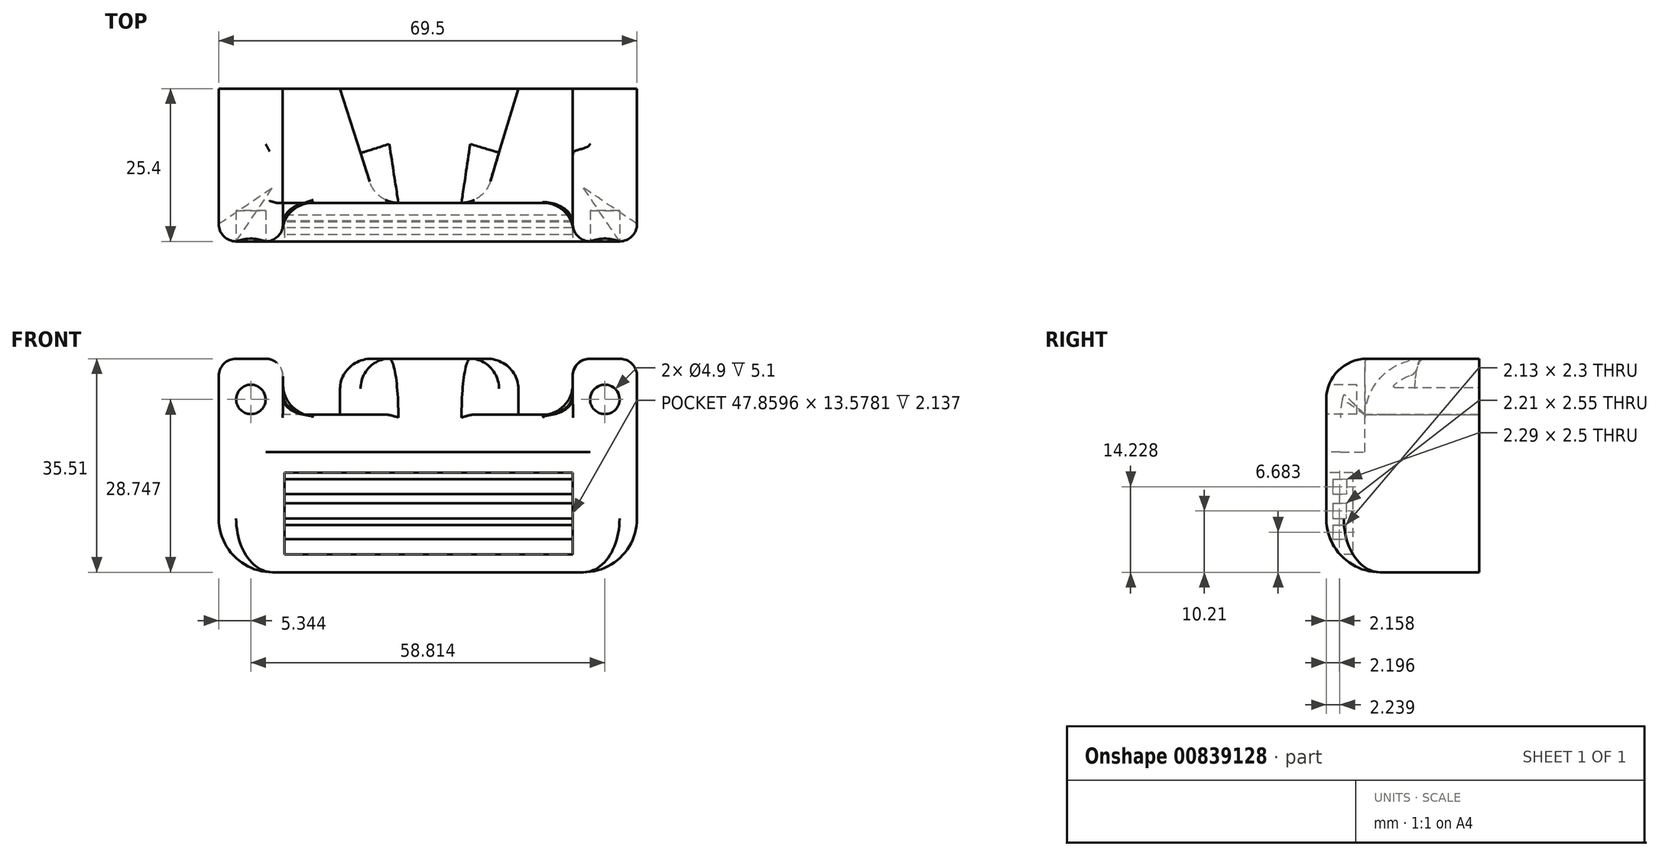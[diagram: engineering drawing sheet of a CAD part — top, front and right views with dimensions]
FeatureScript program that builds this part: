
annotation { "Feature Type Name" : "Feature", "Feature Type Description" : "" }
export const myFeature = defineFeature(function(context is Context, id is Id, definition is map)
    precondition{}
    {
        {
            var Q0;
            Q0=qCreatedBy(makeId("Front.planeOp"),FACE);
            var sketch = newSketch(context, id + "F0", { "sketchPlane" : qUnion([Q0])});
            skLineSegment(sketch, "E0.bottom", {"start": v(-27.6, 7.03) * mm, "end": v(41.91, 7.03) * mm});
            skLineSegment(sketch, "E0.top", {"start": v(-27.6, -12.98) * mm, "end": v(41.91, -12.98) * mm});
            skLineSegment(sketch, "E0.left", {"start": v(-27.6, 7.03) * mm, "end": v(-27.6, -12.98) * mm});
            skLineSegment(sketch, "E0.right", {"start": v(41.91, 7.03) * mm, "end": v(41.91, -12.98) * mm});
            skSolve(sketch);
        }
        {
            var Q0;
            Q0=makeQuery(id+"F0.imprint","IMPRINT",FACE,{"disambiguationData":[TD([[makeQuery(id+"F0.imprint","IMPRINT",EDGE,{"derivedFrom":sQuery(id+"F0.wireOp",EDGE,"E0.bottom")}),-1.0]])]});
            extrude(context, id + "F1", {"entities" : qUnion([Q0]), "depth" : 25.4 * mm, "offsetDistance" : 25.4 * mm});
        }
        {
            var Q0;
            Q0=makeQuery(id+"F1.opExtrude","SWEPT_FACE",FACE,{"disambiguationData":[OSD([sQuery(id+"F0.wireOp",EDGE,"E0.bottom")])]});
            var sketch = newSketch(context, id + "F2", { "sketchPlane" : qUnion([Q0])});
            skLineSegment(sketch, "E1.bottom", {"start": v(-16.9, 0) * mm, "end": v(31.22, 0) * mm});
            skLineSegment(sketch, "E1.top", {"start": v(-16.9, -19) * mm, "end": v(31.22, -19) * mm});
            skLineSegment(sketch, "E1.left", {"start": v(-16.9, 0) * mm, "end": v(-16.9, -19) * mm});
            skLineSegment(sketch, "E1.right", {"start": v(31.22, 0) * mm, "end": v(31.22, -19) * mm});
            skLineSegment(sketch, "E2.bottom", {"start": v(-27.6, 0) * mm, "end": v(-16.9, 0) * mm});
            skLineSegment(sketch, "E2.top", {"start": v(-27.6, -25.4) * mm, "end": v(-16.9, -25.4) * mm});
            skLineSegment(sketch, "E2.left", {"start": v(-27.6, 0) * mm, "end": v(-27.6, -25.4) * mm});
            skLineSegment(sketch, "E2.right", {"start": v(-16.9, 0) * mm, "end": v(-16.9, -25.4) * mm});
            skLineSegment(sketch, "E3.bottom", {"start": v(31.22, 0) * mm, "end": v(41.91, 0) * mm});
            skLineSegment(sketch, "E3.top", {"start": v(31.22, -25.4) * mm, "end": v(41.91, -25.4) * mm});
            skLineSegment(sketch, "E3.left", {"start": v(31.22, 0) * mm, "end": v(31.22, -25.4) * mm});
            skLineSegment(sketch, "E3.right", {"start": v(41.91, 0) * mm, "end": v(41.91, -25.4) * mm});
            skSolve(sketch);
        }
        {
            var Q0;
            {var subQ1=sQuery(id+"F2.wireOp",EDGE,"E2.bottom");Q0=makeQuery(id+"F2.imprint","IMPRINT",FACE,{"disambiguationData":[TD([[makeQuery(id+"F2.imprint","IMPRINT",EDGE,{"derivedFrom":subQ1}),-1.0]])]});}
            var Q1;
            {var subQ0=sQuery(id+"F2.wireOp",EDGE,"E1.bottom");Q1=makeQuery(id+"F2.imprint","IMPRINT",FACE,{"disambiguationData":[TD([[makeQuery(id+"F2.imprint","IMPRINT",EDGE,{"derivedFrom":subQ0}),-1.0]])]});}
            var Q2;
            {var subQ3=sQuery(id+"F2.wireOp",EDGE,"E3.bottom");Q2=makeQuery(id+"F2.imprint","IMPRINT",FACE,{"disambiguationData":[TD([[makeQuery(id+"F2.imprint","IMPRINT",EDGE,{"derivedFrom":subQ3}),-1.0]])]});}
            extrude(context, id + "F3", {"entities" : qUnion([Q0, Q1, Q2]), "operationType" : NewBodyOperationType.ADD, "depth" : 15.5 * mm, "offsetDistance" : 25.4 * mm});
        }
        {
            var Q0;
            Q0=makeQuery(id+"F3.opExtrude","CAP_EDGE",EDGE,{"disambiguationData":[OSD([sQuery(id+"F2.wireOp",EDGE,"E2.top")])],"isStart":false});
            var Q1;
            Q1=makeQuery(id+"F3.opExtrude","CAP_EDGE",EDGE,{"disambiguationData":[OSD([sQuery(id+"F2.wireOp",EDGE,"E3.top")])],"isStart":false});
            fillet(context, id + "F4", {"entities" : qUnion([Q0, Q1]), "radius" : 6.76 * mm, "tangentPropagation" : true, "allowEdgeOverflow" : false});
        }
        {
            var Q0;
            Q0=makeQuery(id+"F4.opFillet","BLEND_EDGE",EDGE,{"blendedFrom":[makeQuery(id+"F3.opExtrude","CAP_EDGE",EDGE,{"disambiguationData":[OSD([sQuery(id+"F2.wireOp",EDGE,"E2.top")])],"isStart":false}),makeQuery(id+"F3.boolean.opBoolean","MERGE",FACE,{"derivedFrom":[makeQuery(id+"F1.opExtrude","SWEPT_FACE",FACE,{"disambiguationData":[OSD([sQuery(id+"F0.wireOp",EDGE,"E0.left")])]}),makeQuery(id+"F3.opExtrude","SWEPT_FACE",FACE,{"disambiguationData":[OSD([sQuery(id+"F2.wireOp",EDGE,"E2.left")])]})]})],"blendedInto":[makeQuery(id+"F3.boolean.opBoolean","MERGE",FACE,{"derivedFrom":[makeQuery(id+"F1.opExtrude","SWEPT_FACE",FACE,{"disambiguationData":[OSD([sQuery(id+"F0.wireOp",EDGE,"E0.left")])]}),makeQuery(id+"F3.opExtrude","SWEPT_FACE",FACE,{"disambiguationData":[OSD([sQuery(id+"F2.wireOp",EDGE,"E2.left")])]})]})]});
            var Q1;
            Q1=makeQuery(id+"F3.boolean.opBoolean","MERGE",EDGE,{"derivedFrom":[makeQuery(id+"F1.opExtrude","CAP_EDGE",EDGE,{"disambiguationData":[OSD([sQuery(id+"F0.wireOp",EDGE,"E0.right")])],"isStart":false}),makeQuery(id+"F3.opExtrude","SWEPT_EDGE",EDGE,{"disambiguationData":[OSD([sQuery(id+"F2.wireOp",EDGE,"E3.top"),sQuery(id+"F2.wireOp",EDGE,"E3.right")])]})]});
            fillet(context, id + "F5", {"entities" : qUnion([Q0, Q1]), "radius" : 2.9 * mm, "tangentPropagation" : true, "allowEdgeOverflow" : false});
        }
        {
            var Q0;
            Q0=makeQuery(id+"F4.opFillet","BLEND_EDGE",EDGE,{"blendedFrom":[makeQuery(id+"F3.opExtrude","CAP_EDGE",EDGE,{"disambiguationData":[OSD([sQuery(id+"F2.wireOp",EDGE,"E2.top")])],"isStart":false}),makeQuery(id+"F3.opExtrude","SWEPT_FACE",FACE,{"disambiguationData":[OSD([sQuery(id+"F2.wireOp",EDGE,"E1.top")])]})],"blendedInto":[makeQuery(id+"F3.opExtrude","SWEPT_FACE",FACE,{"disambiguationData":[OSD([sQuery(id+"F2.wireOp",EDGE,"E1.top")])]})]});
            fillet(context, id + "F6", {"entities" : qUnion([Q0]), "radius" : 9.79 * mm, "tangentPropagation" : true, "allowEdgeOverflow" : false});
        }
        {
            var Q0;
            Q0=makeQuery(id+"F4.opFillet","BLEND_EDGE",EDGE,{"blendedFrom":[makeQuery(id+"F3.opExtrude","CAP_EDGE",EDGE,{"disambiguationData":[OSD([sQuery(id+"F2.wireOp",EDGE,"E2.top")])],"isStart":false}),makeQuery(id+"F3.opExtrude","SWEPT_FACE",FACE,{"disambiguationData":[OSD([sQuery(id+"F2.wireOp",EDGE,"E2.right")])]})],"blendedInto":[makeQuery(id+"F3.opExtrude","SWEPT_FACE",FACE,{"disambiguationData":[OSD([sQuery(id+"F2.wireOp",EDGE,"E2.right")])]})]});
            var Q1;
            Q1=makeQuery(id+"F4.opFillet","BLEND_EDGE",EDGE,{"blendedFrom":[makeQuery(id+"F3.opExtrude","CAP_EDGE",EDGE,{"disambiguationData":[OSD([sQuery(id+"F2.wireOp",EDGE,"E2.top")])],"isStart":false}),makeQuery(id+"F3.opExtrude","SWEPT_FACE",FACE,{"disambiguationData":[OSD([sQuery(id+"F2.wireOp",EDGE,"E3.left")])]})],"blendedInto":[makeQuery(id+"F3.opExtrude","SWEPT_FACE",FACE,{"disambiguationData":[OSD([sQuery(id+"F2.wireOp",EDGE,"E3.left")])]})]});
            fillet(context, id + "F7", {"entities" : qUnion([Q0, Q1]), "radius" : 2.9 * mm, "tangentPropagation" : true, "allowEdgeOverflow" : false});
        }
        {
            var Q0;
            Q0=makeQuery(id+"F3.opExtrude","CAP_FACE",FACE,{"disambiguationData":[OSD([sQuery(id+"F2.wireOp",EDGE,"E1.bottom"),sQuery(id+"F2.wireOp",EDGE,"E1.top"),sQuery(id+"F2.wireOp",EDGE,"E2.bottom"),sQuery(id+"F2.wireOp",EDGE,"E2.top"),sQuery(id+"F2.wireOp",EDGE,"E2.left"),sQuery(id+"F2.wireOp",EDGE,"E2.right"),sQuery(id+"F2.wireOp",EDGE,"E3.bottom"),sQuery(id+"F2.wireOp",EDGE,"E3.top"),sQuery(id+"F2.wireOp",EDGE,"E3.left"),sQuery(id+"F2.wireOp",EDGE,"E3.right")])],"isStart":false});
            var sketch = newSketch(context, id + "F8", { "sketchPlane" : qUnion([Q0])});
            skLineSegment(sketch, "E4", {"start": v(-7.43, 0) * mm, "end": v(-1.4, -19) * mm});
            skLineSegment(sketch, "E5", {"start": v(-1.4, -19) * mm, "end": v(-16.95, -19) * mm});
            skLineSegment(sketch, "E6", {"start": v(-16.95, -19) * mm, "end": v(-16.95, 0) * mm});
            skLineSegment(sketch, "E7", {"start": v(-16.95, 0) * mm, "end": v(-7.43, 0) * mm});
            skLineSegment(sketch, "E8", {"start": v(16.46, -19) * mm, "end": v(22.19, 0) * mm});
            skLineSegment(sketch, "E9", {"start": v(16.46, -19) * mm, "end": v(31.2, -19) * mm});
            skLineSegment(sketch, "E10", {"start": v(31.2, -19) * mm, "end": v(31.2, 0) * mm});
            skLineSegment(sketch, "E11", {"start": v(31.2, 0) * mm, "end": v(22.19, 0) * mm});
            skSolve(sketch);
        }
        {
            var Q0;
            {var subQ0=sQuery(id+"F8.wireOp",EDGE,"E7");Q0=makeQuery(id+"F8.imprint","IMPRINT",FACE,{"disambiguationData":[TD([[makeQuery(id+"F8.imprint","IMPRINT",EDGE,{"derivedFrom":subQ0}),-1.0]])]});}
            var Q1;
            {var subQ0=sQuery(id+"F8.wireOp",EDGE,"E5");Q1=makeQuery(id+"F8.imprint","IMPRINT",FACE,{"disambiguationData":[TD([[makeQuery(id+"F8.imprint","IMPRINT",EDGE,{"derivedFrom":subQ0}),-1.0]])]});}
            var Q2;
            {var subQ0=sQuery(id+"F8.wireOp",EDGE,"E9");Q2=makeQuery(id+"F8.imprint","IMPRINT",FACE,{"disambiguationData":[TD([[makeQuery(id+"F8.imprint","IMPRINT",EDGE,{"derivedFrom":subQ0}),1.0]])]});}
            var Q3;
            {var subQ0=sQuery(id+"F8.wireOp",EDGE,"E11");Q3=makeQuery(id+"F8.imprint","IMPRINT",FACE,{"disambiguationData":[TD([[makeQuery(id+"F8.imprint","IMPRINT",EDGE,{"derivedFrom":subQ0}),-1.0]])]});}
            extrude(context, id + "F9", {"entities" : qUnion([Q0, Q1, Q2, Q3]), "operationType" : NewBodyOperationType.REMOVE, "oppositeDirection" : true, "depth" : 9.3 * mm, "offsetDistance" : 25 * mm});
        }
        {
            var Q0;
            Q0=makeQuery(id+"F9.boolean.opBoolean","COPY",EDGE,{"derivedFrom":makeQuery(id+"F9.opExtrude","CAP_EDGE",EDGE,{"disambiguationData":[OSD([sQuery(id+"F8.wireOp",EDGE,"E10")])],"isStart":true})});
            var Q1;
            Q1=makeQuery(id+"F9.boolean.opBoolean","INTERSECT",EDGE,{"derivedFrom":[makeQuery(id+"F6.opFillet","BLEND_FACE",FACE,{"disambiguationData":[OSD([sQuery(id+"F2.wireOp",EDGE,"E1.top"),sQuery(id+"F2.wireOp",EDGE,"E2.top")])]}),makeQuery(id+"F9.opExtrude","SWEPT_FACE",FACE,{"disambiguationData":[OSD([sQuery(id+"F8.wireOp",EDGE,"E10")])]})]});
            var Q2;
            Q2=makeQuery(id+"F9.boolean.opBoolean","COPY",EDGE,{"derivedFrom":makeQuery(id+"F9.opExtrude","CAP_EDGE",EDGE,{"disambiguationData":[OSD([sQuery(id+"F8.wireOp",EDGE,"E6")])],"isStart":true})});
            var Q3;
            Q3=makeQuery(id+"F9.boolean.opBoolean","INTERSECT",EDGE,{"derivedFrom":[makeQuery(id+"F6.opFillet","BLEND_FACE",FACE,{"disambiguationData":[OSD([sQuery(id+"F2.wireOp",EDGE,"E1.top"),sQuery(id+"F2.wireOp",EDGE,"E2.top")])]}),makeQuery(id+"F9.opExtrude","SWEPT_FACE",FACE,{"disambiguationData":[OSD([sQuery(id+"F8.wireOp",EDGE,"E6")])]})]});
            fillet(context, id + "F10", {"entities" : qUnion([Q0, Q1, Q2, Q3]), "radius" : 2.84 * mm, "tangentPropagation" : true, "allowEdgeOverflow" : false});
        }
        {
            var Q0;
            Q0=makeQuery(id+"F9.boolean.opBoolean","COPY",EDGE,{"derivedFrom":makeQuery(id+"F9.opExtrude","CAP_EDGE",EDGE,{"disambiguationData":[OSD([sQuery(id+"F8.wireOp",EDGE,"E4")])],"isStart":true})});
            var Q1;
            Q1=makeQuery(id+"F9.boolean.opBoolean","INTERSECT",EDGE,{"derivedFrom":[makeQuery(id+"F6.opFillet","BLEND_FACE",FACE,{"disambiguationData":[OSD([sQuery(id+"F2.wireOp",EDGE,"E1.top"),sQuery(id+"F2.wireOp",EDGE,"E2.top")])]}),makeQuery(id+"F9.opExtrude","SWEPT_FACE",FACE,{"disambiguationData":[OSD([sQuery(id+"F8.wireOp",EDGE,"E4")])]})]});
            var Q2;
            Q2=makeQuery(id+"F9.boolean.opBoolean","COPY",EDGE,{"derivedFrom":makeQuery(id+"F9.opExtrude","CAP_EDGE",EDGE,{"disambiguationData":[OSD([sQuery(id+"F8.wireOp",EDGE,"E8")])],"isStart":true})});
            var Q3;
            Q3=makeQuery(id+"F9.boolean.opBoolean","INTERSECT",EDGE,{"derivedFrom":[makeQuery(id+"F6.opFillet","BLEND_FACE",FACE,{"disambiguationData":[OSD([sQuery(id+"F2.wireOp",EDGE,"E1.top"),sQuery(id+"F2.wireOp",EDGE,"E2.top")])]}),makeQuery(id+"F9.opExtrude","SWEPT_FACE",FACE,{"disambiguationData":[OSD([sQuery(id+"F8.wireOp",EDGE,"E8")])]})]});
            fillet(context, id + "F11", {"entities" : qUnion([Q0, Q1, Q2, Q3]), "radius" : 5 * mm, "tangentPropagation" : true, "allowEdgeOverflow" : false});
        }
        {
            var Q0;
            Q0=makeQuery(id+"F9.boolean.opBoolean","INTERSECT",EDGE,{"derivedFrom":[makeQuery(id+"F6.opFillet","BLEND_FACE",FACE,{"disambiguationData":[OSD([sQuery(id+"F2.wireOp",EDGE,"E1.top"),sQuery(id+"F2.wireOp",EDGE,"E2.top")])]}),makeQuery(id+"F9.opExtrude","CAP_FACE",FACE,{"disambiguationData":[OSD([sQuery(id+"F8.wireOp",EDGE,"E4"),sQuery(id+"F8.wireOp",EDGE,"E5"),sQuery(id+"F8.wireOp",EDGE,"E6"),sQuery(id+"F8.wireOp",EDGE,"E7")])],"isStart":false})]});
            var Q1;
            Q1=makeQuery(id+"F9.boolean.opBoolean","INTERSECT",EDGE,{"derivedFrom":[makeQuery(id+"F6.opFillet","BLEND_FACE",FACE,{"disambiguationData":[OSD([sQuery(id+"F2.wireOp",EDGE,"E1.top"),sQuery(id+"F2.wireOp",EDGE,"E2.top")])]}),makeQuery(id+"F9.opExtrude","CAP_FACE",FACE,{"disambiguationData":[OSD([sQuery(id+"F8.wireOp",EDGE,"E8"),sQuery(id+"F8.wireOp",EDGE,"E9"),sQuery(id+"F8.wireOp",EDGE,"E10"),sQuery(id+"F8.wireOp",EDGE,"E11")])],"isStart":false})]});
            fillet(context, id + "F12", {"entities" : qUnion([Q0, Q1]), "radius" : 0.49 * mm, "tangentPropagation" : true, "allowEdgeOverflow" : false});
        }
        {
            var Q0;
            Q0=makeQuery(id+"F3.boolean.opBoolean","MERGE",FACE,{"derivedFrom":[makeQuery(id+"F1.opExtrude","CAP_FACE",FACE,{"disambiguationData":[OSD([sQuery(id+"F0.wireOp",EDGE,"E0.bottom"),sQuery(id+"F0.wireOp",EDGE,"E0.top"),sQuery(id+"F0.wireOp",EDGE,"E0.left"),sQuery(id+"F0.wireOp",EDGE,"E0.right")])],"isStart":false}),makeQuery(id+"F3.opExtrude","SWEPT_FACE",FACE,{"disambiguationData":[OSD([sQuery(id+"F2.wireOp",EDGE,"E2.top")])]}),makeQuery(id+"F3.opExtrude","SWEPT_FACE",FACE,{"disambiguationData":[OSD([sQuery(id+"F2.wireOp",EDGE,"E3.top")])]})]});
            var sketch = newSketch(context, id + "F13", { "sketchPlane" : qUnion([Q0])});
            skLineSegment(sketch, "E12.bottom", {"start": v(-16.66, 3.59) * mm, "end": v(31.2, 3.59) * mm});
            skLineSegment(sketch, "E12.top", {"start": v(-16.66, -9.99) * mm, "end": v(31.2, -9.99) * mm});
            skLineSegment(sketch, "E12.left", {"start": v(-16.66, 3.59) * mm, "end": v(-16.66, -9.99) * mm});
            skLineSegment(sketch, "E12.right", {"start": v(31.2, 3.59) * mm, "end": v(31.2, -9.99) * mm});
            skSolve(sketch);
        }
        {
            var Q0;
            Q0=makeQuery(id+"F13.imprint","IMPRINT",FACE,{"disambiguationData":[TD([[makeQuery(id+"F13.imprint","IMPRINT",EDGE,{"derivedFrom":sQuery(id+"F13.wireOp",EDGE,"E12.bottom")}),-1.0]])]});
            extrude(context, id + "F14", {"entities" : qUnion([Q0]), "operationType" : NewBodyOperationType.REMOVE, "oppositeDirection" : true, "depth" : 4.4 * mm, "offsetDistance" : 25 * mm});
        }
        {
            var Q0;
            Q0=makeQuery(id+"F1.opExtrude","CAP_EDGE",EDGE,{"disambiguationData":[OSD([sQuery(id+"F0.wireOp",EDGE,"E0.top")])],"isStart":false});
            fillet(context, id + "F15", {"entities" : qUnion([Q0]), "radius" : 8.93 * mm, "tangentPropagation" : true, "allowEdgeOverflow" : false});
        }
        {
            var Q0;
            Q0=makeQuery(id+"F3.opExtrude","SWEPT_EDGE",EDGE,{"disambiguationData":[OSD([sQuery(id+"F2.wireOp",EDGE,"E1.top"),sQuery(id+"F2.wireOp",EDGE,"E2.right")])]});
            var Q1;
            Q1=makeQuery(id+"F3.opExtrude","SWEPT_EDGE",EDGE,{"disambiguationData":[OSD([sQuery(id+"F2.wireOp",EDGE,"E1.top"),sQuery(id+"F2.wireOp",EDGE,"E3.left")])]});
            fillet(context, id + "F16", {"entities" : qUnion([Q0, Q1]), "radius" : 5 * mm, "tangentPropagation" : true, "allowEdgeOverflow" : false});
        }
        {
            var Q0;
            Q0=makeQuery(id+"F14.boolean.opBoolean","COPY",FACE,{"derivedFrom":makeQuery(id+"F14.opExtrude","SWEPT_FACE",FACE,{"disambiguationData":[OSD([sQuery(id+"F13.wireOp",EDGE,"E12.left")])]})});
            var sketch = newSketch(context, id + "F17", { "sketchPlane" : qUnion([Q0])});
            skLineSegment(sketch, "E13.bottom", {"start": v(-24.3, 2.5) * mm, "end": v(-22.01, 2.5) * mm});
            skLineSegment(sketch, "E13.top", {"start": v(-24.3, 0) * mm, "end": v(-22.01, 0) * mm});
            skLineSegment(sketch, "E13.left", {"start": v(-24.3, 2.5) * mm, "end": v(-24.3, 0) * mm});
            skLineSegment(sketch, "E13.right", {"start": v(-22.01, 2.5) * mm, "end": v(-22.01, 0) * mm});
            skLineSegment(sketch, "E14.bottom", {"start": v(-24.3, -1.5) * mm, "end": v(-22.1, -1.5) * mm});
            skLineSegment(sketch, "E14.top", {"start": v(-24.3, -4.05) * mm, "end": v(-22.1, -4.05) * mm});
            skLineSegment(sketch, "E14.left", {"start": v(-24.3, -1.5) * mm, "end": v(-24.3, -4.05) * mm});
            skLineSegment(sketch, "E14.right", {"start": v(-22.1, -1.5) * mm, "end": v(-22.1, -4.05) * mm});
            skLineSegment(sketch, "E15.bottom", {"start": v(-24.3, -5.15) * mm, "end": v(-22.18, -5.15) * mm});
            skLineSegment(sketch, "E15.top", {"start": v(-24.3, -7.45) * mm, "end": v(-22.18, -7.45) * mm});
            skLineSegment(sketch, "E15.left", {"start": v(-24.3, -5.15) * mm, "end": v(-24.3, -7.45) * mm});
            skLineSegment(sketch, "E15.right", {"start": v(-22.18, -5.15) * mm, "end": v(-22.18, -7.45) * mm});
            skSolve(sketch);
        }
        {
            var Q0;
            Q0=makeQuery(id+"F17.imprint","IMPRINT",FACE,{"disambiguationData":[TD([[makeQuery(id+"F17.imprint","IMPRINT",EDGE,{"derivedFrom":sQuery(id+"F17.wireOp",EDGE,"E13.bottom")}),-1.0]])]});
            var Q1;
            Q1=makeQuery(id+"F17.imprint","IMPRINT",FACE,{"disambiguationData":[TD([[makeQuery(id+"F17.imprint","IMPRINT",EDGE,{"derivedFrom":sQuery(id+"F17.wireOp",EDGE,"E14.bottom")}),-1.0]])]});
            var Q2;
            Q2=makeQuery(id+"F17.imprint","IMPRINT",FACE,{"disambiguationData":[TD([[makeQuery(id+"F17.imprint","IMPRINT",EDGE,{"derivedFrom":sQuery(id+"F17.wireOp",EDGE,"E15.bottom")}),-1.0]])]});
            extrude(context, id + "F18", {"entities" : qUnion([Q0, Q1, Q2]), "operationType" : NewBodyOperationType.ADD, "depth" : 49.5 * mm, "offsetDistance" : 25 * mm});
        }
        {
            var Q0;
            Q0=makeQuery(id+"F3.boolean.opBoolean","MERGE",FACE,{"derivedFrom":[makeQuery(id+"F1.opExtrude","CAP_FACE",FACE,{"disambiguationData":[OSD([sQuery(id+"F0.wireOp",EDGE,"E0.bottom"),sQuery(id+"F0.wireOp",EDGE,"E0.top"),sQuery(id+"F0.wireOp",EDGE,"E0.left"),sQuery(id+"F0.wireOp",EDGE,"E0.right")])],"isStart":false}),makeQuery(id+"F3.opExtrude","SWEPT_FACE",FACE,{"disambiguationData":[OSD([sQuery(id+"F2.wireOp",EDGE,"E2.top")])]}),makeQuery(id+"F3.opExtrude","SWEPT_FACE",FACE,{"disambiguationData":[OSD([sQuery(id+"F2.wireOp",EDGE,"E3.top")])]})]});
            var sketch = newSketch(context, id + "F19", { "sketchPlane" : qUnion([Q0])});
            skCircle(sketch, "E16", {"center": v(-22.25, 15.77) * mm, "radius": 2.45 * mm});
            skCircle(sketch, "E17", {"center": v(36.57, 15.77) * mm, "radius": 2.45 * mm});
            skSolve(sketch);
        }
        {
            var Q0;
            {var subQ1=sQuery(id+"F2.wireOp",EDGE,"E2.top");var subQ2=sQuery(id+"F0.wireOp",EDGE,"E0.left");var subQ3=sQuery(id+"F0.wireOp",EDGE,"E0.bottom");var subQ4=makeQuery(id+"F3.boolean.opBoolean","MERGE",FACE,{"derivedFrom":[makeQuery(id+"F1.opExtrude","CAP_FACE",FACE,{"disambiguationData":[OSD([subQ3,sQuery(id+"F0.wireOp",EDGE,"E0.top"),subQ2,sQuery(id+"F0.wireOp",EDGE,"E0.right")])],"isStart":false}),makeQuery(id+"F3.opExtrude","SWEPT_FACE",FACE,{"disambiguationData":[OSD([subQ1])]}),makeQuery(id+"F3.opExtrude","SWEPT_FACE",FACE,{"disambiguationData":[OSD([sQuery(id+"F2.wireOp",EDGE,"E3.top")])]})]});var subQ6=makeQuery(id+"F4.opFillet","BLEND_EDGE",EDGE,{"disambiguationData":[OD(0.0)],"blendedFrom":[makeQuery(id+"F3.opExtrude","CAP_EDGE",EDGE,{"disambiguationData":[OSD([subQ1])],"isStart":false}),subQ4],"blendedInto":[subQ4]});Q0=makeQuery(id+"F19.imprint","IMPRINT",FACE,{"disambiguationData":[TD([[makeQuery(id+"F19.imprint","IMPRINT",EDGE,{"derivedFrom":subQ6}),-1.0]])]});}
            var Q1;
            {var subQ1=sQuery(id+"F2.wireOp",EDGE,"E2.top");var subQ2=sQuery(id+"F0.wireOp",EDGE,"E0.left");var subQ3=sQuery(id+"F0.wireOp",EDGE,"E0.bottom");var subQ4=makeQuery(id+"F3.boolean.opBoolean","MERGE",FACE,{"derivedFrom":[makeQuery(id+"F1.opExtrude","CAP_FACE",FACE,{"disambiguationData":[OSD([subQ3,sQuery(id+"F0.wireOp",EDGE,"E0.top"),subQ2,sQuery(id+"F0.wireOp",EDGE,"E0.right")])],"isStart":false}),makeQuery(id+"F3.opExtrude","SWEPT_FACE",FACE,{"disambiguationData":[OSD([subQ1])]}),makeQuery(id+"F3.opExtrude","SWEPT_FACE",FACE,{"disambiguationData":[OSD([sQuery(id+"F2.wireOp",EDGE,"E3.top")])]})]});var subQ6=makeQuery(id+"F4.opFillet","BLEND_EDGE",EDGE,{"disambiguationData":[OD(0.0)],"blendedFrom":[makeQuery(id+"F3.opExtrude","CAP_EDGE",EDGE,{"disambiguationData":[OSD([subQ1])],"isStart":false}),subQ4],"blendedInto":[subQ4]});Q1=makeQuery(id+"F19.imprint","IMPRINT",FACE,{"disambiguationData":[TD([[makeQuery(id+"F19.imprint","IMPRINT",EDGE,{"derivedFrom":subQ6}),1.0]])]});}
            var Q2;
            {var subQ1=sQuery(id+"F2.wireOp",EDGE,"E3.top");var subQ2=sQuery(id+"F2.wireOp",EDGE,"E2.top");var subQ3=sQuery(id+"F0.wireOp",EDGE,"E0.right");var subQ4=sQuery(id+"F0.wireOp",EDGE,"E0.bottom");var subQ5=makeQuery(id+"F3.boolean.opBoolean","MERGE",FACE,{"derivedFrom":[makeQuery(id+"F1.opExtrude","CAP_FACE",FACE,{"disambiguationData":[OSD([subQ4,sQuery(id+"F0.wireOp",EDGE,"E0.top"),sQuery(id+"F0.wireOp",EDGE,"E0.left"),subQ3])],"isStart":false}),makeQuery(id+"F3.opExtrude","SWEPT_FACE",FACE,{"disambiguationData":[OSD([subQ2])]}),makeQuery(id+"F3.opExtrude","SWEPT_FACE",FACE,{"disambiguationData":[OSD([subQ1])]})]});var subQ7=makeQuery(id+"F4.opFillet","BLEND_EDGE",EDGE,{"disambiguationData":[OD(1.0)],"blendedFrom":[makeQuery(id+"F3.opExtrude","CAP_EDGE",EDGE,{"disambiguationData":[OSD([subQ2])],"isStart":false}),subQ5],"blendedInto":[subQ5]});Q2=makeQuery(id+"F19.imprint","IMPRINT",FACE,{"disambiguationData":[TD([[makeQuery(id+"F19.imprint","IMPRINT",EDGE,{"derivedFrom":subQ7}),-1.0]])]});}
            var Q3;
            {var subQ1=sQuery(id+"F2.wireOp",EDGE,"E3.top");var subQ2=sQuery(id+"F2.wireOp",EDGE,"E2.top");var subQ3=sQuery(id+"F0.wireOp",EDGE,"E0.right");var subQ4=sQuery(id+"F0.wireOp",EDGE,"E0.bottom");var subQ5=makeQuery(id+"F3.boolean.opBoolean","MERGE",FACE,{"derivedFrom":[makeQuery(id+"F1.opExtrude","CAP_FACE",FACE,{"disambiguationData":[OSD([subQ4,sQuery(id+"F0.wireOp",EDGE,"E0.top"),sQuery(id+"F0.wireOp",EDGE,"E0.left"),subQ3])],"isStart":false}),makeQuery(id+"F3.opExtrude","SWEPT_FACE",FACE,{"disambiguationData":[OSD([subQ2])]}),makeQuery(id+"F3.opExtrude","SWEPT_FACE",FACE,{"disambiguationData":[OSD([subQ1])]})]});var subQ7=makeQuery(id+"F4.opFillet","BLEND_EDGE",EDGE,{"disambiguationData":[OD(1.0)],"blendedFrom":[makeQuery(id+"F3.opExtrude","CAP_EDGE",EDGE,{"disambiguationData":[OSD([subQ2])],"isStart":false}),subQ5],"blendedInto":[subQ5]});Q3=makeQuery(id+"F19.imprint","IMPRINT",FACE,{"disambiguationData":[TD([[makeQuery(id+"F19.imprint","IMPRINT",EDGE,{"derivedFrom":subQ7}),1.0]])]});}
            extrude(context, id + "F20", {"entities" : qUnion([Q0, Q1, Q2, Q3]), "operationType" : NewBodyOperationType.REMOVE, "oppositeDirection" : true, "depth" : 5.1 * mm, "offsetDistance" : 25 * mm});
        }
    });
